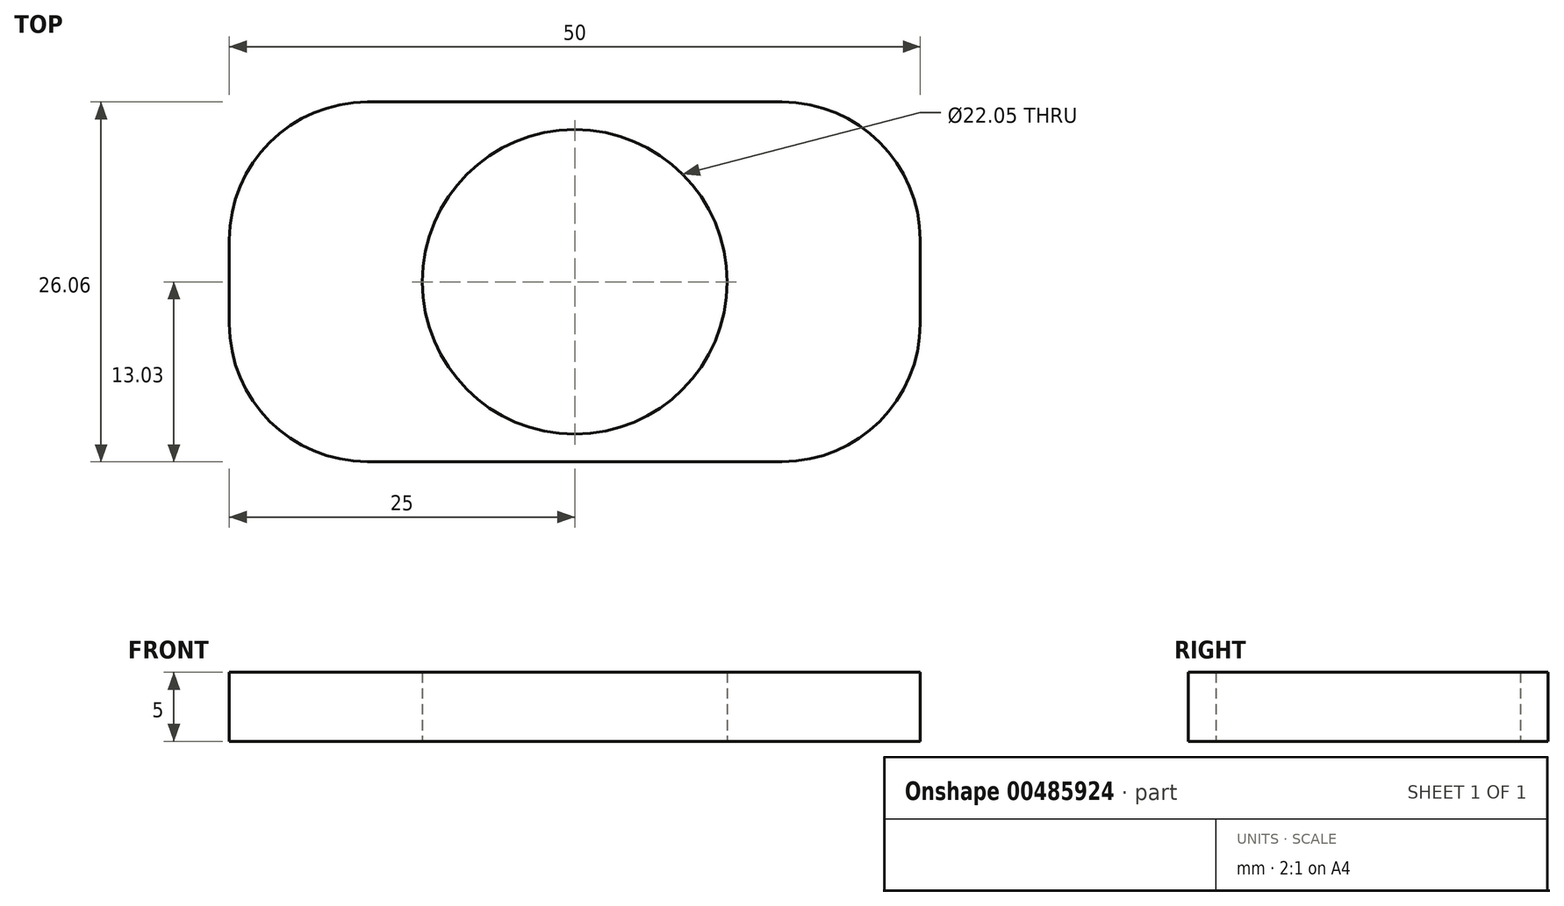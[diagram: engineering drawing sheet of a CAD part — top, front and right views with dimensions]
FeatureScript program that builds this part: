
annotation { "Feature Type Name" : "Feature", "Feature Type Description" : "" }
export const myFeature = defineFeature(function(context is Context, id is Id, definition is map)
    precondition{}
    {
        {
            var Q0;
            Q0=qCreatedBy(makeId("Top.planeOp"),FACE);
            var sketch = newSketch(context, id + "F0", { "sketchPlane" : qUnion([Q0])});
            skCircle(sketch, "E0", {"center": v(0, 0) * mm, "radius": 13.03 * mm});
            skLineSegment(sketch, "E1.bottom", {"start": v(0, 13.03) * mm, "end": v(25, 13.03) * mm});
            skLineSegment(sketch, "E1.top", {"start": v(0, -13.03) * mm, "end": v(25, -13.03) * mm});
            skLineSegment(sketch, "E1.right", {"start": v(25, 13.03) * mm, "end": v(25, -13.02) * mm});
            skLineSegment(sketch, "E2.MirrorCS", {"start": v(0, 13.03) * mm, "end": v(-25, 13.02) * mm});
            skLineSegment(sketch, "E3.MirrorCS", {"start": v(0, -13.02) * mm, "end": v(-25, -13.03) * mm});
            skLineSegment(sketch, "E4.MirrorCS", {"start": v(-25, 13.03) * mm, "end": v(-25, -13.02) * mm});
            skCircle(sketch, "E5", {"center": v(0, 0) * mm, "radius": 11.03 * mm});
            skSolve(sketch);
        }
        {
            var Q0;
            {var subQ0=sQuery(id+"F0.wireOp",EDGE,"E2.MirrorCS");Q0=makeQuery(id+"F0.imprint","IMPRINT",FACE,{"disambiguationData":[TD([[makeQuery(id+"F0.imprint","IMPRINT",EDGE,{"derivedFrom":subQ0}),1.0]])]});}
            var Q1;
            {var subQ0=sQuery(id+"F0.wireOp",EDGE,"E1.bottom");Q1=makeQuery(id+"F0.imprint","IMPRINT",FACE,{"disambiguationData":[TD([[makeQuery(id+"F0.imprint","IMPRINT",EDGE,{"derivedFrom":subQ0}),-1.0]])]});}
            var Q2;
            Q2=makeQuery(id+"F0.imprint","IMPRINT",FACE,{"disambiguationData":[TD([[makeQuery(id+"F0.imprint","IMPRINT",EDGE,{"derivedFrom":sQuery(id+"F0.wireOp",EDGE,"E5")}),-1.0]])]});
            extrude(context, id + "F1", {"entities" : qUnion([Q0, Q1, Q2]), "endBound" : BoundingType.SYMMETRIC, "depth" : 5 * mm});
        }
        {
            var Q0;
            Q0=qCreatedBy(makeId("Right.planeOp"),FACE);
            var sketch = newSketch(context, id + "F2", { "sketchPlane" : qUnion([Q0])});
            skLineSegment(sketch, "E6.0", {"start": v(-11.03, 2.5) * mm, "end": v(11.03, 2.5) * mm});
            skLineSegment(sketch, "E7.0", {"start": v(-11.03, -2.5) * mm, "end": v(11.03, -2.5) * mm});
            skLineSegment(sketch, "E8", {"start": v(0, 2.5) * mm, "end": v(6.4, 2.5) * mm, "construction": true});
            skLineSegment(sketch, "E9", {"start": v(6.4, 2.5) * mm, "end": v(6.4, -2.5) * mm, "construction": true});
            skLineSegment(sketch, "E10", {"start": v(6.25, 2.5) * mm, "end": v(6.25, -2.5) * mm, "construction": true});
            skFitSpline(sketch, "E11", {"points": [v(6.4, 2.5) * mm, v(6.25, 0) * mm, v(6.4, -2.5) * mm], "startDerivative": vector(-1.2, -5) * mm, "endDerivative": vector(1.2, -5) * mm});
            skLineSegment(sketch, "E12", {"start": v(6.4, 2.5) * mm, "end": v(5.43, 2.5) * mm});
            skLineSegment(sketch, "E13", {"start": v(5.43, 2.5) * mm, "end": v(5.43, -2.5) * mm});
            skLineSegment(sketch, "E14", {"start": v(5.43, -2.5) * mm, "end": v(6.4, -2.5) * mm});
            skLineSegment(sketch, "E15", {"start": v(0, 0) * mm, "end": v(0, 10.22) * mm, "construction": true});
            skSolve(sketch);
        }
        {
            var Q0;
            {var subQ0=sQuery(id+"F2.wireOp",EDGE,"E11");Q0=makeQuery(id+"F2.imprint","IMPRINT",FACE,{"disambiguationData":[TD([[makeQuery(id+"F2.imprint","IMPRINT",EDGE,{"derivedFrom":subQ0}),-1.0]])]});}
            var Q1;
            Q1=sQuery(id+"F2.wireOp",EDGE,"E15");
            revolve(context, id + "F3", {"operationType" : NewBodyOperationType.REMOVE, "entities" : qUnion([Q0]), "axis" : qUnion([Q1]), "revolveType" : RevolveType.FULL, "oppositeDirection" : true});
        }
        {
            var Q0;
            Q0=makeQuery(id+"F1.opExtrude","SWEPT_EDGE",EDGE,{"disambiguationData":[OSD([sQuery(id+"F0.wireOp",EDGE,"E3.MirrorCS"),sQuery(id+"F0.wireOp",EDGE,"E4.MirrorCS")])]});
            var Q1;
            Q1=makeQuery(id+"F1.opExtrude","SWEPT_EDGE",EDGE,{"disambiguationData":[OSD([sQuery(id+"F0.wireOp",EDGE,"E2.MirrorCS"),sQuery(id+"F0.wireOp",EDGE,"E4.MirrorCS")])]});
            var Q2;
            Q2=makeQuery(id+"F1.opExtrude","SWEPT_EDGE",EDGE,{"disambiguationData":[OSD([sQuery(id+"F0.wireOp",EDGE,"E1.top"),sQuery(id+"F0.wireOp",EDGE,"E1.right")])]});
            var Q3;
            Q3=makeQuery(id+"F1.opExtrude","SWEPT_EDGE",EDGE,{"disambiguationData":[OSD([sQuery(id+"F0.wireOp",EDGE,"E1.bottom"),sQuery(id+"F0.wireOp",EDGE,"E1.right")])]});
            fillet(context, id + "F4", {"entities" : qUnion([Q0, Q1, Q2, Q3]), "radius" : 10 * mm, "tangentPropagation" : true, "allowEdgeOverflow" : false});
        }
    });
